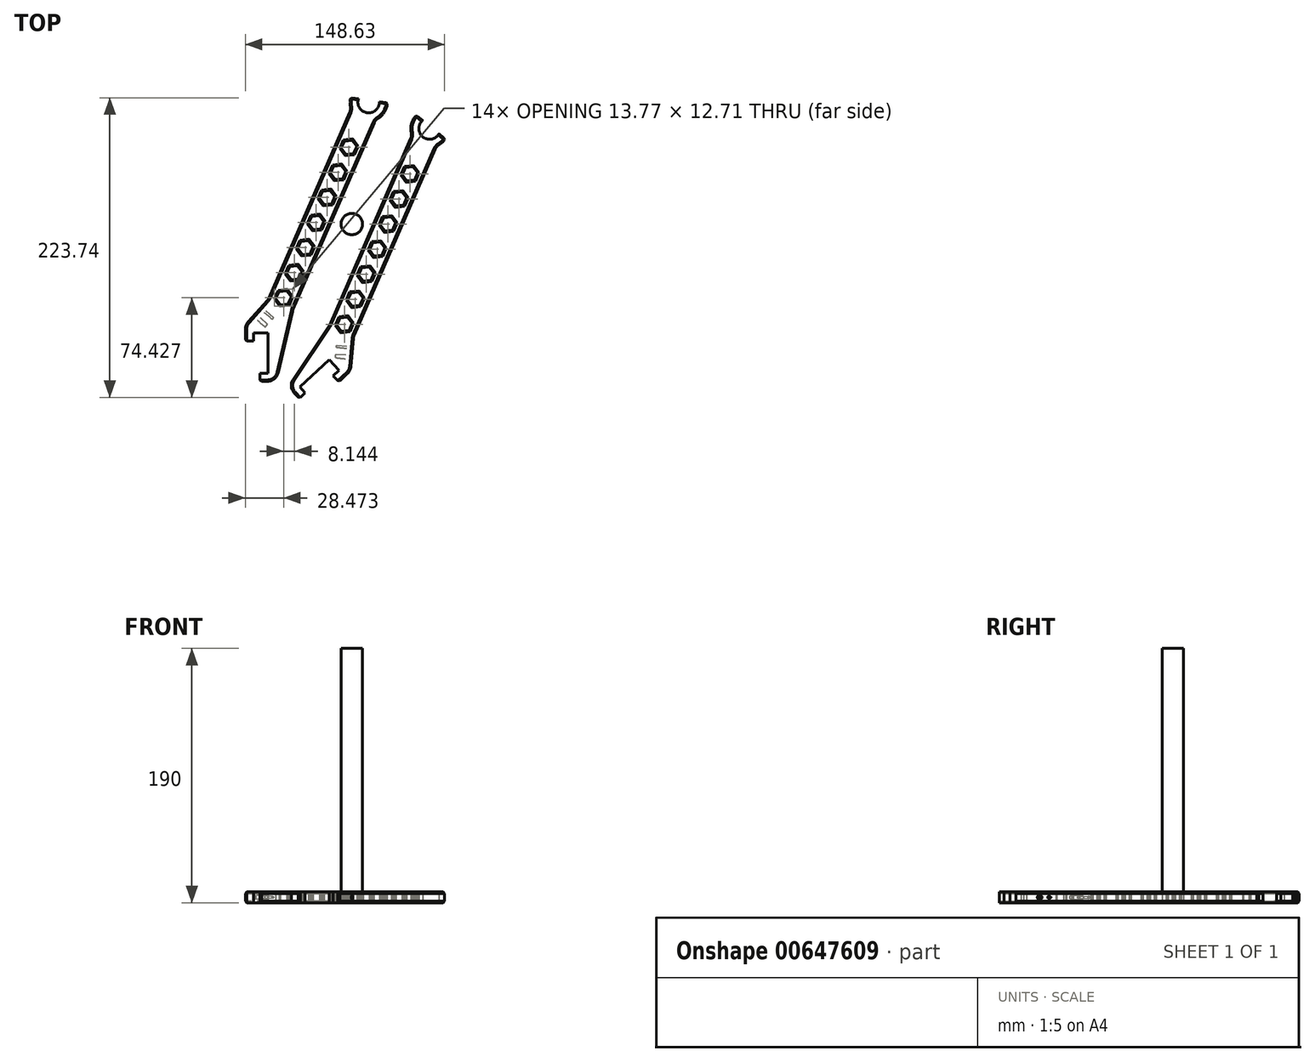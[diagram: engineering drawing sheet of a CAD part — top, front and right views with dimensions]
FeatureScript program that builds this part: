
annotation { "Feature Type Name" : "Feature", "Feature Type Description" : "" }
export const myFeature = defineFeature(function(context is Context, id is Id, definition is map)
    precondition{}
    {
        {
            var Q0;
            Q0=qCreatedBy(makeId("Top.planeOp"),FACE);
            var sketch = newSketch(context, id + "F0", { "sketchPlane" : qUnion([Q0])});
            skLineSegment(sketch, "E0.bottom", {"start": v(6, 6) * mm, "end": v(-17, 6) * mm, "construction": true});
            skLineSegment(sketch, "E0.top", {"start": v(6, -36) * mm, "end": v(-6, -36) * mm});
            skLineSegment(sketch, "E0.left", {"start": v(6, 6) * mm, "end": v(6, -36) * mm, "construction": true});
            skLineSegment(sketch, "E0.right", {"start": v(-17, 6) * mm, "end": v(-17, -6) * mm});
            skLineSegment(sketch, "E1", {"start": v(-17, -6) * mm, "end": v(-11, -6) * mm});
            skLineSegment(sketch, "E2", {"start": v(-11, -6) * mm, "end": v(-11, 0) * mm});
            skLineSegment(sketch, "E3", {"start": v(-11, 0) * mm, "end": v(0, 0) * mm});
            skLineSegment(sketch, "E4", {"start": v(0, 0) * mm, "end": v(0, -30) * mm});
            skLineSegment(sketch, "E5", {"start": v(0, -30) * mm, "end": v(-6, -30) * mm});
            skLineSegment(sketch, "E6", {"start": v(-6, -30) * mm, "end": v(-6, -36) * mm});
            skCircle(sketch, "E7", {"center": v(75, 172.5) * mm, "radius": 8 * mm});
            skCircle(sketch, "E8", {"center": v(75, 172.5) * mm, "radius": 14 * mm});
            skLineSegment(sketch, "E9", {"start": v(61.4, 175.82) * mm, "end": v(89, 172.07) * mm});
            skLineSegment(sketch, "E10", {"start": v(-17, 6) * mm, "end": v(0, 25.08) * mm});
            skLineSegment(sketch, "E11", {"start": v(0, 25.08) * mm, "end": v(61.92, 167.5) * mm});
            skLineSegment(sketch, "E12", {"start": v(18.34, 17.1) * mm, "end": v(6, -36) * mm});
            skLineSegment(sketch, "E13", {"start": v(18.34, 17.1) * mm, "end": v(80.26, 159.53) * mm});
            skLineSegment(sketch, "E14.0", {"start": v(0, 0) * mm, "end": v(75, 172.5) * mm, "construction": true});
            skLineSegment(sketch, "E15", {"start": v(0, 25.08) * mm, "end": v(18.34, 17.1) * mm, "construction": true});
            skCircle(sketch, "E16.cCircle", {"center": v(60.34, 138.78) * mm, "radius": 5.77 * mm, "construction": true});
            skLineSegment(sketch, "E16.0", {"start": v(58.04, 133.48) * mm, "end": v(54.6, 138.12) * mm});
            skLineSegment(sketch, "E16.1", {"start": v(54.6, 138.12) * mm, "end": v(56.9, 143.42) * mm});
            skLineSegment(sketch, "E16.2", {"start": v(56.9, 143.42) * mm, "end": v(62.64, 144.07) * mm});
            skLineSegment(sketch, "E16.3", {"start": v(62.64, 144.07) * mm, "end": v(66.07, 139.43) * mm});
            skLineSegment(sketch, "E16.4", {"start": v(66.07, 139.43) * mm, "end": v(63.77, 134.14) * mm});
            skLineSegment(sketch, "E16.5", {"start": v(63.77, 134.14) * mm, "end": v(58.04, 133.48) * mm});
            skCircle(sketch, "E17.cCircle", {"center": v(44.05, 101.31) * mm, "radius": 5.77 * mm, "construction": true});
            skLineSegment(sketch, "E17.0", {"start": v(41.75, 96.02) * mm, "end": v(38.31, 100.66) * mm});
            skLineSegment(sketch, "E17.1", {"start": v(38.31, 100.66) * mm, "end": v(40.61, 105.95) * mm});
            skLineSegment(sketch, "E17.2", {"start": v(40.61, 105.95) * mm, "end": v(46.35, 106.6) * mm});
            skLineSegment(sketch, "E17.3", {"start": v(46.35, 106.6) * mm, "end": v(49.79, 101.97) * mm});
            skLineSegment(sketch, "E17.4", {"start": v(49.79, 101.97) * mm, "end": v(47.48, 96.67) * mm});
            skLineSegment(sketch, "E17.5", {"start": v(47.48, 96.67) * mm, "end": v(41.75, 96.02) * mm});
            skCircle(sketch, "E18.cCircle", {"center": v(35.9, 82.58) * mm, "radius": 5.77 * mm, "construction": true});
            skLineSegment(sketch, "E18.0", {"start": v(33.6, 77.29) * mm, "end": v(30.17, 81.93) * mm});
            skLineSegment(sketch, "E18.1", {"start": v(30.17, 81.93) * mm, "end": v(32.47, 87.22) * mm});
            skLineSegment(sketch, "E18.2", {"start": v(32.47, 87.22) * mm, "end": v(38.2, 87.88) * mm});
            skLineSegment(sketch, "E18.3", {"start": v(38.2, 87.88) * mm, "end": v(41.64, 83.24) * mm});
            skLineSegment(sketch, "E18.4", {"start": v(41.64, 83.24) * mm, "end": v(39.34, 77.94) * mm});
            skLineSegment(sketch, "E18.5", {"start": v(39.34, 77.94) * mm, "end": v(33.6, 77.29) * mm});
            skCircle(sketch, "E19.cCircle", {"center": v(11.47, 26.39) * mm, "radius": 5.77 * mm, "construction": true});
            skLineSegment(sketch, "E19.0", {"start": v(9.17, 21.1) * mm, "end": v(5.74, 25.73) * mm});
            skLineSegment(sketch, "E19.1", {"start": v(5.74, 25.73) * mm, "end": v(8.04, 31.03) * mm});
            skLineSegment(sketch, "E19.2", {"start": v(8.04, 31.03) * mm, "end": v(13.77, 31.68) * mm});
            skLineSegment(sketch, "E19.3", {"start": v(13.77, 31.68) * mm, "end": v(17.2, 27.04) * mm});
            skLineSegment(sketch, "E19.4", {"start": v(17.2, 27.04) * mm, "end": v(14.9, 21.75) * mm});
            skLineSegment(sketch, "E19.5", {"start": v(14.9, 21.75) * mm, "end": v(9.17, 21.1) * mm});
            skLineSegment(sketch, "E20", {"start": v(62.64, 144.07) * mm, "end": v(71.81, 165.16) * mm, "construction": true});
            skLineSegment(sketch, "E21", {"start": v(9.17, 21.1) * mm, "end": v(0, 0) * mm, "construction": true});
            skCircle(sketch, "E22.cCircle", {"center": v(19.62, 45.12) * mm, "radius": 5.77 * mm, "construction": true});
            skLineSegment(sketch, "E22.0", {"start": v(21.92, 50.41) * mm, "end": v(25.35, 45.77) * mm});
            skLineSegment(sketch, "E22.1", {"start": v(25.35, 45.77) * mm, "end": v(23.05, 40.48) * mm});
            skLineSegment(sketch, "E22.2", {"start": v(23.05, 40.48) * mm, "end": v(17.31, 39.82) * mm});
            skLineSegment(sketch, "E22.3", {"start": v(17.31, 39.82) * mm, "end": v(13.88, 44.47) * mm});
            skLineSegment(sketch, "E22.4", {"start": v(13.88, 44.47) * mm, "end": v(16.18, 49.76) * mm});
            skLineSegment(sketch, "E22.5", {"start": v(16.18, 49.76) * mm, "end": v(21.92, 50.41) * mm});
            skCircle(sketch, "E23.cCircle", {"center": v(27.76, 63.85) * mm, "radius": 5.77 * mm, "construction": true});
            skLineSegment(sketch, "E23.0", {"start": v(30.06, 69.14) * mm, "end": v(33.5, 64.5) * mm});
            skLineSegment(sketch, "E23.1", {"start": v(33.5, 64.5) * mm, "end": v(31.2, 59.2) * mm});
            skLineSegment(sketch, "E23.2", {"start": v(31.2, 59.2) * mm, "end": v(25.46, 58.56) * mm});
            skLineSegment(sketch, "E23.3", {"start": v(25.46, 58.56) * mm, "end": v(22.02, 63.2) * mm});
            skLineSegment(sketch, "E23.4", {"start": v(22.02, 63.2) * mm, "end": v(24.33, 68.5) * mm});
            skLineSegment(sketch, "E23.5", {"start": v(24.33, 68.5) * mm, "end": v(30.06, 69.14) * mm});
            skCircle(sketch, "E24.cCircle", {"center": v(52.2, 120.04) * mm, "radius": 5.77 * mm, "construction": true});
            skLineSegment(sketch, "E24.0", {"start": v(49.9, 114.75) * mm, "end": v(46.46, 119.4) * mm});
            skLineSegment(sketch, "E24.1", {"start": v(46.46, 119.4) * mm, "end": v(48.76, 124.69) * mm});
            skLineSegment(sketch, "E24.2", {"start": v(48.76, 124.69) * mm, "end": v(54.5, 125.34) * mm});
            skLineSegment(sketch, "E24.3", {"start": v(54.5, 125.34) * mm, "end": v(57.93, 120.7) * mm});
            skLineSegment(sketch, "E24.4", {"start": v(57.93, 120.7) * mm, "end": v(55.63, 115.4) * mm});
            skLineSegment(sketch, "E24.5", {"start": v(55.63, 115.4) * mm, "end": v(49.9, 114.75) * mm});
            skLineSegment(sketch, "E25", {"start": v(60.34, 138.78) * mm, "end": v(52.2, 120.04) * mm, "construction": true});
            skLineSegment(sketch, "E26", {"start": v(52.2, 120.04) * mm, "end": v(44.05, 101.31) * mm, "construction": true});
            skLineSegment(sketch, "E27", {"start": v(44.05, 101.31) * mm, "end": v(35.9, 82.58) * mm, "construction": true});
            skLineSegment(sketch, "E28", {"start": v(35.9, 82.58) * mm, "end": v(27.76, 63.85) * mm, "construction": true});
            skLineSegment(sketch, "E29", {"start": v(27.76, 63.85) * mm, "end": v(19.62, 45.12) * mm, "construction": true});
            skLineSegment(sketch, "E30", {"start": v(19.62, 45.12) * mm, "end": v(11.47, 26.39) * mm, "construction": true});
            skSolve(sketch);
        }
        {
            var Q0;
            Q0=makeQuery(id+"F0.imprint","IMPRINT",FACE,{"disambiguationData":[TD([[makeQuery(id+"F0.imprint","IMPRINT",EDGE,{"derivedFrom":sQuery(id+"F0.wireOp",EDGE,"E0.top")}),-1.0]])]});
            var Q1;
            {var subQ0=sQuery(id+"F0.wireOp",EDGE,"E9");var subQ6=sQuery(id+"F0.wireOp",EDGE,"E7");var subQ7=makeQuery(id+"F0.imprint","INTERSECT",VERTEX,{"disambiguationData":[OD(0.0)],"derivedFrom":[subQ6,subQ0]});Q1=makeQuery(id+"F0.imprint","IMPRINT",FACE,{"disambiguationData":[TD([[makeQuery(id+"F0.imprint","IMPRINT",EDGE,{"disambiguationData":[TD([[subQ7,-1.0]])],"derivedFrom":subQ6}),-1.0]])]});}
            extrude(context, id + "F1", {"entities" : qUnion([Q0, Q1]), "depth" : 8 * mm, "offsetDistance" : 25 * mm});
        }
        {
            var Q0;
            Q0=makeQuery(id+"F1.opExtrude","SWEPT_EDGE",EDGE,{"disambiguationData":[OSD([sQuery(id+"F0.wireOp",EDGE,"E0.right"),sQuery(id+"F0.wireOp",EDGE,"E10")])]});
            var Q1;
            Q1=makeQuery(id+"F1.opExtrude","SWEPT_EDGE",EDGE,{"disambiguationData":[OSD([sQuery(id+"F0.wireOp",EDGE,"E10"),sQuery(id+"F0.wireOp",EDGE,"E11")])]});
            var Q2;
            Q2=makeQuery(id+"F1.opExtrude","SWEPT_EDGE",EDGE,{"disambiguationData":[OSD([sQuery(id+"F0.wireOp",EDGE,"E8"),sQuery(id+"F0.wireOp",EDGE,"E11")])]});
            var Q3;
            Q3=makeQuery(id+"F1.opExtrude","SWEPT_EDGE",EDGE,{"disambiguationData":[OSD([sQuery(id+"F0.wireOp",EDGE,"E8"),sQuery(id+"F0.wireOp",EDGE,"E13")])]});
            var Q4;
            Q4=makeQuery(id+"F1.opExtrude","SWEPT_EDGE",EDGE,{"disambiguationData":[OSD([sQuery(id+"F0.wireOp",EDGE,"E12"),sQuery(id+"F0.wireOp",EDGE,"E13")])]});
            var Q5;
            Q5=makeQuery(id+"F1.opExtrude","SWEPT_EDGE",EDGE,{"disambiguationData":[OSD([sQuery(id+"F0.wireOp",EDGE,"E0.top"),sQuery(id+"F0.wireOp",EDGE,"E12")])]});
            fillet(context, id + "F2", {"entities" : qUnion([Q0, Q1, Q2, Q3, Q4, Q5]), "radius" : 8 * mm, "tangentPropagation" : true, "allowEdgeOverflow" : false});
        }
        {
            var Q0;
            Q0=makeQuery(id+"F1.opExtrude","SWEPT_FACE",FACE,{"disambiguationData":[OSD([sQuery(id+"F0.wireOp",EDGE,"E10")])]});
            var sketch = newSketch(context, id + "F3", { "sketchPlane" : qUnion([Q0])});
            skCircle(sketch, "E31", {"center": v(-10.44, 4) * mm, "radius": 0.97 * mm});
            skCircle(sketch, "E32", {"center": v(-3.22, 4) * mm, "radius": 1.6 * mm});
            skLineSegment(sketch, "E33", {"start": v(3.78, 4) * mm, "end": v(-17.44, 4) * mm, "construction": true});
            skSolve(sketch);
        }
        {
            var Q0;
            Q0=makeQuery(id+"F3.imprint","IMPRINT",FACE,{"disambiguationData":[TD([[makeQuery(id+"F3.imprint","IMPRINT",EDGE,{"derivedFrom":sQuery(id+"F3.wireOp",EDGE,"E32")}),1.0]])]});
            var Q1;
            Q1=makeQuery(id+"F3.imprint","IMPRINT",FACE,{"disambiguationData":[TD([[makeQuery(id+"F3.imprint","IMPRINT",EDGE,{"derivedFrom":sQuery(id+"F3.wireOp",EDGE,"E31")}),1.0]])]});
            extrude(context, id + "F4", {"entities" : qUnion([Q0, Q1]), "operationType" : NewBodyOperationType.REMOVE, "oppositeDirection" : true, "depth" : 12 * mm, "offsetDistance" : 25 * mm, "hasDraft" : true, "draftAngle" : 1 * degree, "draftPullDirection" : true});
        }
        {
            var Q0;
            {var subQ0=sQuery(id+"F0.wireOp",EDGE,"E9");Q0=makeQuery(id+"F1.opExtrude","CAP_EDGE",EDGE,{"disambiguationData":[OSD([subQ0]),TDD([makeQuery(id+"F0.imprint","IMPRINT",EDGE,{"disambiguationData":[TD([[makeQuery(id+"F0.imprint","INTERSECT",VERTEX,{"disambiguationData":[OD(0.0)],"derivedFrom":[sQuery(id+"F0.wireOp",EDGE,"E8"),subQ0]}),-1.0]])],"derivedFrom":subQ0})])],"isStart":false});}
            var Q1;
            {var subQ0=sQuery(id+"F0.wireOp",EDGE,"E9");Q1=makeQuery(id+"F1.opExtrude","CAP_EDGE",EDGE,{"disambiguationData":[OSD([subQ0]),TDD([makeQuery(id+"F0.imprint","IMPRINT",EDGE,{"disambiguationData":[TD([[makeQuery(id+"F0.imprint","INTERSECT",VERTEX,{"disambiguationData":[OD(1.0)],"derivedFrom":[sQuery(id+"F0.wireOp",EDGE,"E8"),subQ0]}),1.0]])],"derivedFrom":subQ0})])],"isStart":false});}
            var Q2;
            {var subQ0=sQuery(id+"F0.wireOp",EDGE,"E8");Q2=makeQuery(id+"F1.opExtrude","CAP_EDGE",EDGE,{"disambiguationData":[OSD([subQ0]),TDD([makeQuery(id+"F0.imprint","IMPRINT",EDGE,{"disambiguationData":[TD([[makeQuery(id+"F0.imprint","INTERSECT",VERTEX,{"disambiguationData":[OD(1.0)],"derivedFrom":[subQ0,sQuery(id+"F0.wireOp",EDGE,"E9")]}),1.0]])],"derivedFrom":subQ0})])],"isStart":false});}
            var Q3;
            {var subQ0=sQuery(id+"F0.wireOp",EDGE,"E8");Q3=makeQuery(id+"F1.opExtrude","CAP_EDGE",EDGE,{"disambiguationData":[OSD([subQ0]),TDD([makeQuery(id+"F0.imprint","IMPRINT",EDGE,{"disambiguationData":[TD([[makeQuery(id+"F0.imprint","INTERSECT",VERTEX,{"disambiguationData":[OD(0.0)],"derivedFrom":[subQ0,sQuery(id+"F0.wireOp",EDGE,"E9")]}),-1.0]])],"derivedFrom":subQ0})])],"isStart":false});}
            var Q4;
            Q4=makeQuery(id+"F1.opExtrude","CAP_EDGE",EDGE,{"disambiguationData":[OSD([sQuery(id+"F0.wireOp",EDGE,"E16.2")])],"isStart":false});
            var Q5;
            Q5=makeQuery(id+"F1.opExtrude","CAP_EDGE",EDGE,{"disambiguationData":[OSD([sQuery(id+"F0.wireOp",EDGE,"E16.3")])],"isStart":false});
            var Q6;
            Q6=makeQuery(id+"F1.opExtrude","CAP_EDGE",EDGE,{"disambiguationData":[OSD([sQuery(id+"F0.wireOp",EDGE,"E16.4")])],"isStart":false});
            var Q7;
            Q7=makeQuery(id+"F1.opExtrude","CAP_EDGE",EDGE,{"disambiguationData":[OSD([sQuery(id+"F0.wireOp",EDGE,"E16.5")])],"isStart":false});
            var Q8;
            Q8=makeQuery(id+"F1.opExtrude","CAP_EDGE",EDGE,{"disambiguationData":[OSD([sQuery(id+"F0.wireOp",EDGE,"E16.0")])],"isStart":false});
            var Q9;
            Q9=makeQuery(id+"F1.opExtrude","CAP_EDGE",EDGE,{"disambiguationData":[OSD([sQuery(id+"F0.wireOp",EDGE,"E16.1")])],"isStart":false});
            var Q10;
            Q10=makeQuery(id+"F1.opExtrude","CAP_EDGE",EDGE,{"disambiguationData":[OSD([sQuery(id+"F0.wireOp",EDGE,"E17.2")])],"isStart":false});
            var Q11;
            Q11=makeQuery(id+"F1.opExtrude","CAP_EDGE",EDGE,{"disambiguationData":[OSD([sQuery(id+"F0.wireOp",EDGE,"E17.3")])],"isStart":false});
            var Q12;
            Q12=makeQuery(id+"F1.opExtrude","CAP_EDGE",EDGE,{"disambiguationData":[OSD([sQuery(id+"F0.wireOp",EDGE,"E17.4")])],"isStart":false});
            var Q13;
            Q13=makeQuery(id+"F1.opExtrude","CAP_EDGE",EDGE,{"disambiguationData":[OSD([sQuery(id+"F0.wireOp",EDGE,"E17.5")])],"isStart":false});
            var Q14;
            Q14=makeQuery(id+"F1.opExtrude","CAP_EDGE",EDGE,{"disambiguationData":[OSD([sQuery(id+"F0.wireOp",EDGE,"E17.0")])],"isStart":false});
            var Q15;
            Q15=makeQuery(id+"F1.opExtrude","CAP_EDGE",EDGE,{"disambiguationData":[OSD([sQuery(id+"F0.wireOp",EDGE,"E17.1")])],"isStart":false});
            var Q16;
            Q16=makeQuery(id+"F1.opExtrude","CAP_EDGE",EDGE,{"disambiguationData":[OSD([sQuery(id+"F0.wireOp",EDGE,"E18.3")])],"isStart":false});
            var Q17;
            Q17=makeQuery(id+"F1.opExtrude","CAP_EDGE",EDGE,{"disambiguationData":[OSD([sQuery(id+"F0.wireOp",EDGE,"E18.4")])],"isStart":false});
            var Q18;
            Q18=makeQuery(id+"F1.opExtrude","CAP_EDGE",EDGE,{"disambiguationData":[OSD([sQuery(id+"F0.wireOp",EDGE,"E18.5")])],"isStart":false});
            var Q19;
            Q19=makeQuery(id+"F1.opExtrude","CAP_EDGE",EDGE,{"disambiguationData":[OSD([sQuery(id+"F0.wireOp",EDGE,"E18.0")])],"isStart":false});
            var Q20;
            Q20=makeQuery(id+"F1.opExtrude","CAP_EDGE",EDGE,{"disambiguationData":[OSD([sQuery(id+"F0.wireOp",EDGE,"E18.1")])],"isStart":false});
            var Q21;
            Q21=makeQuery(id+"F1.opExtrude","CAP_EDGE",EDGE,{"disambiguationData":[OSD([sQuery(id+"F0.wireOp",EDGE,"E18.2")])],"isStart":false});
            var Q22;
            Q22=makeQuery(id+"F1.opExtrude","CAP_EDGE",EDGE,{"disambiguationData":[OSD([sQuery(id+"F0.wireOp",EDGE,"E19.2")])],"isStart":false});
            var Q23;
            Q23=makeQuery(id+"F1.opExtrude","CAP_EDGE",EDGE,{"disambiguationData":[OSD([sQuery(id+"F0.wireOp",EDGE,"E19.3")])],"isStart":false});
            var Q24;
            Q24=makeQuery(id+"F1.opExtrude","CAP_EDGE",EDGE,{"disambiguationData":[OSD([sQuery(id+"F0.wireOp",EDGE,"E19.4")])],"isStart":false});
            var Q25;
            Q25=makeQuery(id+"F1.opExtrude","CAP_EDGE",EDGE,{"disambiguationData":[OSD([sQuery(id+"F0.wireOp",EDGE,"E19.5")])],"isStart":false});
            var Q26;
            Q26=makeQuery(id+"F1.opExtrude","CAP_EDGE",EDGE,{"disambiguationData":[OSD([sQuery(id+"F0.wireOp",EDGE,"E19.0")])],"isStart":false});
            var Q27;
            Q27=makeQuery(id+"F1.opExtrude","CAP_EDGE",EDGE,{"disambiguationData":[OSD([sQuery(id+"F0.wireOp",EDGE,"E19.1")])],"isStart":false});
            var Q28;
            {var subQ0=sQuery(id+"F0.wireOp",EDGE,"E9");Q28=makeQuery(id+"F1.opExtrude","CAP_EDGE",EDGE,{"disambiguationData":[OSD([subQ0]),TDD([makeQuery(id+"F0.imprint","IMPRINT",EDGE,{"disambiguationData":[TD([[makeQuery(id+"F0.imprint","INTERSECT",VERTEX,{"disambiguationData":[OD(0.0)],"derivedFrom":[sQuery(id+"F0.wireOp",EDGE,"E8"),subQ0]}),-1.0]])],"derivedFrom":subQ0})])],"isStart":true});}
            var Q29;
            {var subQ0=sQuery(id+"F0.wireOp",EDGE,"E9");Q29=makeQuery(id+"F1.opExtrude","CAP_EDGE",EDGE,{"disambiguationData":[OSD([subQ0]),TDD([makeQuery(id+"F0.imprint","IMPRINT",EDGE,{"disambiguationData":[TD([[makeQuery(id+"F0.imprint","INTERSECT",VERTEX,{"disambiguationData":[OD(1.0)],"derivedFrom":[sQuery(id+"F0.wireOp",EDGE,"E8"),subQ0]}),1.0]])],"derivedFrom":subQ0})])],"isStart":true});}
            var Q30;
            {var subQ0=sQuery(id+"F0.wireOp",EDGE,"E8");Q30=makeQuery(id+"F1.opExtrude","CAP_EDGE",EDGE,{"disambiguationData":[OSD([subQ0]),TDD([makeQuery(id+"F0.imprint","IMPRINT",EDGE,{"disambiguationData":[TD([[makeQuery(id+"F0.imprint","INTERSECT",VERTEX,{"disambiguationData":[OD(1.0)],"derivedFrom":[subQ0,sQuery(id+"F0.wireOp",EDGE,"E9")]}),1.0]])],"derivedFrom":subQ0})])],"isStart":true});}
            var Q31;
            {var subQ0=sQuery(id+"F0.wireOp",EDGE,"E8");Q31=makeQuery(id+"F1.opExtrude","CAP_EDGE",EDGE,{"disambiguationData":[OSD([subQ0]),TDD([makeQuery(id+"F0.imprint","IMPRINT",EDGE,{"disambiguationData":[TD([[makeQuery(id+"F0.imprint","INTERSECT",VERTEX,{"disambiguationData":[OD(0.0)],"derivedFrom":[subQ0,sQuery(id+"F0.wireOp",EDGE,"E9")]}),-1.0]])],"derivedFrom":subQ0})])],"isStart":true});}
            var Q32;
            Q32=makeQuery(id+"F1.opExtrude","CAP_EDGE",EDGE,{"disambiguationData":[OSD([sQuery(id+"F0.wireOp",EDGE,"E16.3")])],"isStart":true});
            var Q33;
            Q33=makeQuery(id+"F1.opExtrude","CAP_EDGE",EDGE,{"disambiguationData":[OSD([sQuery(id+"F0.wireOp",EDGE,"E16.2")])],"isStart":true});
            var Q34;
            Q34=makeQuery(id+"F1.opExtrude","CAP_EDGE",EDGE,{"disambiguationData":[OSD([sQuery(id+"F0.wireOp",EDGE,"E16.1")])],"isStart":true});
            var Q35;
            Q35=makeQuery(id+"F1.opExtrude","CAP_EDGE",EDGE,{"disambiguationData":[OSD([sQuery(id+"F0.wireOp",EDGE,"E16.0")])],"isStart":true});
            var Q36;
            Q36=makeQuery(id+"F1.opExtrude","CAP_EDGE",EDGE,{"disambiguationData":[OSD([sQuery(id+"F0.wireOp",EDGE,"E16.5")])],"isStart":true});
            var Q37;
            Q37=makeQuery(id+"F1.opExtrude","CAP_EDGE",EDGE,{"disambiguationData":[OSD([sQuery(id+"F0.wireOp",EDGE,"E16.4")])],"isStart":true});
            var Q38;
            Q38=makeQuery(id+"F1.opExtrude","CAP_EDGE",EDGE,{"disambiguationData":[OSD([sQuery(id+"F0.wireOp",EDGE,"E17.4")])],"isStart":true});
            var Q39;
            Q39=makeQuery(id+"F1.opExtrude","CAP_EDGE",EDGE,{"disambiguationData":[OSD([sQuery(id+"F0.wireOp",EDGE,"E17.3")])],"isStart":true});
            var Q40;
            Q40=makeQuery(id+"F1.opExtrude","CAP_EDGE",EDGE,{"disambiguationData":[OSD([sQuery(id+"F0.wireOp",EDGE,"E17.2")])],"isStart":true});
            var Q41;
            Q41=makeQuery(id+"F1.opExtrude","CAP_EDGE",EDGE,{"disambiguationData":[OSD([sQuery(id+"F0.wireOp",EDGE,"E17.1")])],"isStart":true});
            var Q42;
            Q42=makeQuery(id+"F1.opExtrude","CAP_EDGE",EDGE,{"disambiguationData":[OSD([sQuery(id+"F0.wireOp",EDGE,"E17.0")])],"isStart":true});
            var Q43;
            Q43=makeQuery(id+"F1.opExtrude","CAP_EDGE",EDGE,{"disambiguationData":[OSD([sQuery(id+"F0.wireOp",EDGE,"E17.5")])],"isStart":true});
            var Q44;
            Q44=makeQuery(id+"F1.opExtrude","CAP_EDGE",EDGE,{"disambiguationData":[OSD([sQuery(id+"F0.wireOp",EDGE,"E18.4")])],"isStart":true});
            var Q45;
            Q45=makeQuery(id+"F1.opExtrude","CAP_EDGE",EDGE,{"disambiguationData":[OSD([sQuery(id+"F0.wireOp",EDGE,"E18.3")])],"isStart":true});
            var Q46;
            Q46=makeQuery(id+"F1.opExtrude","CAP_EDGE",EDGE,{"disambiguationData":[OSD([sQuery(id+"F0.wireOp",EDGE,"E18.2")])],"isStart":true});
            var Q47;
            Q47=makeQuery(id+"F1.opExtrude","CAP_EDGE",EDGE,{"disambiguationData":[OSD([sQuery(id+"F0.wireOp",EDGE,"E18.1")])],"isStart":true});
            var Q48;
            Q48=makeQuery(id+"F1.opExtrude","CAP_EDGE",EDGE,{"disambiguationData":[OSD([sQuery(id+"F0.wireOp",EDGE,"E18.0")])],"isStart":true});
            var Q49;
            Q49=makeQuery(id+"F1.opExtrude","CAP_EDGE",EDGE,{"disambiguationData":[OSD([sQuery(id+"F0.wireOp",EDGE,"E18.5")])],"isStart":true});
            var Q50;
            Q50=makeQuery(id+"F1.opExtrude","CAP_EDGE",EDGE,{"disambiguationData":[OSD([sQuery(id+"F0.wireOp",EDGE,"E19.3")])],"isStart":true});
            var Q51;
            Q51=makeQuery(id+"F1.opExtrude","CAP_EDGE",EDGE,{"disambiguationData":[OSD([sQuery(id+"F0.wireOp",EDGE,"E19.4")])],"isStart":true});
            var Q52;
            Q52=makeQuery(id+"F1.opExtrude","CAP_EDGE",EDGE,{"disambiguationData":[OSD([sQuery(id+"F0.wireOp",EDGE,"E19.5")])],"isStart":true});
            var Q53;
            Q53=makeQuery(id+"F1.opExtrude","CAP_EDGE",EDGE,{"disambiguationData":[OSD([sQuery(id+"F0.wireOp",EDGE,"E19.0")])],"isStart":true});
            var Q54;
            Q54=makeQuery(id+"F1.opExtrude","CAP_EDGE",EDGE,{"disambiguationData":[OSD([sQuery(id+"F0.wireOp",EDGE,"E19.1")])],"isStart":true});
            var Q55;
            Q55=makeQuery(id+"F1.opExtrude","CAP_EDGE",EDGE,{"disambiguationData":[OSD([sQuery(id+"F0.wireOp",EDGE,"E19.2")])],"isStart":true});
            var Q56;
            Q56=makeQuery(id+"F4.boolean.opBoolean","COPY",EDGE,{"derivedFrom":makeQuery(id+"F4.opExtrude","CAP_EDGE",EDGE,{"disambiguationData":[OSD([sQuery(id+"F3.wireOp",EDGE,"E32")])],"isStart":true})});
            var Q57;
            Q57=makeQuery(id+"F4.boolean.opBoolean","COPY",EDGE,{"derivedFrom":makeQuery(id+"F4.opExtrude","CAP_EDGE",EDGE,{"disambiguationData":[OSD([sQuery(id+"F3.wireOp",EDGE,"E31")])],"isStart":true})});
            var Q58;
            Q58=makeQuery(id+"F1.opExtrude","SWEPT_EDGE",EDGE,{"disambiguationData":[OSD([sQuery(id+"F0.wireOp",EDGE,"E0.right"),sQuery(id+"F0.wireOp",EDGE,"E1")])]});
            var Q59;
            Q59=makeQuery(id+"F1.opExtrude","SWEPT_EDGE",EDGE,{"disambiguationData":[OSD([sQuery(id+"F0.wireOp",EDGE,"E0.top"),sQuery(id+"F0.wireOp",EDGE,"E6")])]});
            var Q60;
            {var subQ0=sQuery(id+"F0.wireOp",EDGE,"E9");var subQ1=sQuery(id+"F0.wireOp",EDGE,"E8");Q60=makeQuery(id+"F1.opExtrude","SWEPT_EDGE",EDGE,{"disambiguationData":[OSD([subQ1,subQ0]),TDD([makeQuery(id+"F0.imprint","INTERSECT",VERTEX,{"disambiguationData":[OD(1.0)],"derivedFrom":[subQ1,subQ0]})])]});}
            var Q61;
            {var subQ0=sQuery(id+"F0.wireOp",EDGE,"E9");var subQ1=sQuery(id+"F0.wireOp",EDGE,"E8");Q61=makeQuery(id+"F1.opExtrude","SWEPT_EDGE",EDGE,{"disambiguationData":[OSD([subQ1,subQ0]),TDD([makeQuery(id+"F0.imprint","INTERSECT",VERTEX,{"disambiguationData":[OD(0.0)],"derivedFrom":[subQ1,subQ0]})])]});}
            var Q62;
            Q62=makeQuery(id+"F1.opExtrude","CAP_EDGE",EDGE,{"disambiguationData":[OSD([sQuery(id+"F0.wireOp",EDGE,"E24.2")])],"isStart":false});
            var Q63;
            Q63=makeQuery(id+"F1.opExtrude","CAP_EDGE",EDGE,{"disambiguationData":[OSD([sQuery(id+"F0.wireOp",EDGE,"E24.3")])],"isStart":false});
            var Q64;
            Q64=makeQuery(id+"F1.opExtrude","CAP_EDGE",EDGE,{"disambiguationData":[OSD([sQuery(id+"F0.wireOp",EDGE,"E24.4")])],"isStart":false});
            var Q65;
            Q65=makeQuery(id+"F1.opExtrude","CAP_EDGE",EDGE,{"disambiguationData":[OSD([sQuery(id+"F0.wireOp",EDGE,"E24.5")])],"isStart":false});
            var Q66;
            Q66=makeQuery(id+"F1.opExtrude","CAP_EDGE",EDGE,{"disambiguationData":[OSD([sQuery(id+"F0.wireOp",EDGE,"E24.0")])],"isStart":false});
            var Q67;
            Q67=makeQuery(id+"F1.opExtrude","CAP_EDGE",EDGE,{"disambiguationData":[OSD([sQuery(id+"F0.wireOp",EDGE,"E24.1")])],"isStart":false});
            var Q68;
            Q68=makeQuery(id+"F1.opExtrude","CAP_EDGE",EDGE,{"disambiguationData":[OSD([sQuery(id+"F0.wireOp",EDGE,"E23.0")])],"isStart":false});
            var Q69;
            Q69=makeQuery(id+"F1.opExtrude","CAP_EDGE",EDGE,{"disambiguationData":[OSD([sQuery(id+"F0.wireOp",EDGE,"E23.5")])],"isStart":false});
            var Q70;
            Q70=makeQuery(id+"F1.opExtrude","CAP_EDGE",EDGE,{"disambiguationData":[OSD([sQuery(id+"F0.wireOp",EDGE,"E23.4")])],"isStart":false});
            var Q71;
            Q71=makeQuery(id+"F1.opExtrude","CAP_EDGE",EDGE,{"disambiguationData":[OSD([sQuery(id+"F0.wireOp",EDGE,"E23.3")])],"isStart":false});
            var Q72;
            Q72=makeQuery(id+"F1.opExtrude","CAP_EDGE",EDGE,{"disambiguationData":[OSD([sQuery(id+"F0.wireOp",EDGE,"E23.2")])],"isStart":false});
            var Q73;
            Q73=makeQuery(id+"F1.opExtrude","CAP_EDGE",EDGE,{"disambiguationData":[OSD([sQuery(id+"F0.wireOp",EDGE,"E23.1")])],"isStart":false});
            var Q74;
            Q74=makeQuery(id+"F1.opExtrude","CAP_EDGE",EDGE,{"disambiguationData":[OSD([sQuery(id+"F0.wireOp",EDGE,"E22.0")])],"isStart":false});
            var Q75;
            Q75=makeQuery(id+"F1.opExtrude","CAP_EDGE",EDGE,{"disambiguationData":[OSD([sQuery(id+"F0.wireOp",EDGE,"E22.5")])],"isStart":false});
            var Q76;
            Q76=makeQuery(id+"F1.opExtrude","CAP_EDGE",EDGE,{"disambiguationData":[OSD([sQuery(id+"F0.wireOp",EDGE,"E22.4")])],"isStart":false});
            var Q77;
            Q77=makeQuery(id+"F1.opExtrude","CAP_EDGE",EDGE,{"disambiguationData":[OSD([sQuery(id+"F0.wireOp",EDGE,"E22.3")])],"isStart":false});
            var Q78;
            Q78=makeQuery(id+"F1.opExtrude","CAP_EDGE",EDGE,{"disambiguationData":[OSD([sQuery(id+"F0.wireOp",EDGE,"E22.2")])],"isStart":false});
            var Q79;
            Q79=makeQuery(id+"F1.opExtrude","CAP_EDGE",EDGE,{"disambiguationData":[OSD([sQuery(id+"F0.wireOp",EDGE,"E22.1")])],"isStart":false});
            var Q80;
            Q80=makeQuery(id+"F1.opExtrude","CAP_EDGE",EDGE,{"disambiguationData":[OSD([sQuery(id+"F0.wireOp",EDGE,"E22.4")])],"isStart":true});
            var Q81;
            Q81=makeQuery(id+"F1.opExtrude","CAP_EDGE",EDGE,{"disambiguationData":[OSD([sQuery(id+"F0.wireOp",EDGE,"E22.3")])],"isStart":true});
            var Q82;
            Q82=makeQuery(id+"F1.opExtrude","CAP_EDGE",EDGE,{"disambiguationData":[OSD([sQuery(id+"F0.wireOp",EDGE,"E22.2")])],"isStart":true});
            var Q83;
            Q83=makeQuery(id+"F1.opExtrude","CAP_EDGE",EDGE,{"disambiguationData":[OSD([sQuery(id+"F0.wireOp",EDGE,"E22.1")])],"isStart":true});
            var Q84;
            Q84=makeQuery(id+"F1.opExtrude","CAP_EDGE",EDGE,{"disambiguationData":[OSD([sQuery(id+"F0.wireOp",EDGE,"E22.0")])],"isStart":true});
            var Q85;
            Q85=makeQuery(id+"F1.opExtrude","CAP_EDGE",EDGE,{"disambiguationData":[OSD([sQuery(id+"F0.wireOp",EDGE,"E22.5")])],"isStart":true});
            var Q86;
            Q86=makeQuery(id+"F1.opExtrude","CAP_EDGE",EDGE,{"disambiguationData":[OSD([sQuery(id+"F0.wireOp",EDGE,"E23.3")])],"isStart":true});
            var Q87;
            Q87=makeQuery(id+"F1.opExtrude","CAP_EDGE",EDGE,{"disambiguationData":[OSD([sQuery(id+"F0.wireOp",EDGE,"E23.2")])],"isStart":true});
            var Q88;
            Q88=makeQuery(id+"F1.opExtrude","CAP_EDGE",EDGE,{"disambiguationData":[OSD([sQuery(id+"F0.wireOp",EDGE,"E23.1")])],"isStart":true});
            var Q89;
            Q89=makeQuery(id+"F1.opExtrude","CAP_EDGE",EDGE,{"disambiguationData":[OSD([sQuery(id+"F0.wireOp",EDGE,"E23.0")])],"isStart":true});
            var Q90;
            Q90=makeQuery(id+"F1.opExtrude","CAP_EDGE",EDGE,{"disambiguationData":[OSD([sQuery(id+"F0.wireOp",EDGE,"E23.5")])],"isStart":true});
            var Q91;
            Q91=makeQuery(id+"F1.opExtrude","CAP_EDGE",EDGE,{"disambiguationData":[OSD([sQuery(id+"F0.wireOp",EDGE,"E23.4")])],"isStart":true});
            var Q92;
            Q92=makeQuery(id+"F1.opExtrude","CAP_EDGE",EDGE,{"disambiguationData":[OSD([sQuery(id+"F0.wireOp",EDGE,"E24.5")])],"isStart":true});
            var Q93;
            Q93=makeQuery(id+"F1.opExtrude","CAP_EDGE",EDGE,{"disambiguationData":[OSD([sQuery(id+"F0.wireOp",EDGE,"E24.4")])],"isStart":true});
            var Q94;
            Q94=makeQuery(id+"F1.opExtrude","CAP_EDGE",EDGE,{"disambiguationData":[OSD([sQuery(id+"F0.wireOp",EDGE,"E24.3")])],"isStart":true});
            var Q95;
            Q95=makeQuery(id+"F1.opExtrude","CAP_EDGE",EDGE,{"disambiguationData":[OSD([sQuery(id+"F0.wireOp",EDGE,"E24.2")])],"isStart":true});
            var Q96;
            Q96=makeQuery(id+"F1.opExtrude","CAP_EDGE",EDGE,{"disambiguationData":[OSD([sQuery(id+"F0.wireOp",EDGE,"E24.1")])],"isStart":true});
            var Q97;
            Q97=makeQuery(id+"F1.opExtrude","CAP_EDGE",EDGE,{"disambiguationData":[OSD([sQuery(id+"F0.wireOp",EDGE,"E24.0")])],"isStart":true});
            chamfer(context, id + "F5", {"entities" : qUnion([Q0, Q1, Q2, Q3, Q4, Q5, Q6, Q7, Q8, Q9, Q10, Q11, Q12, Q13, Q14, Q15, Q16, Q17, Q18, Q19, Q20, Q21, Q22, Q23, Q24, Q25, Q26, Q27, Q28, Q29, Q30, Q31, Q32, Q33, Q34, Q35, Q36, Q37, Q38, Q39, Q40, Q41, Q42, Q43, Q44, Q45, Q46, Q47, Q48, Q49, Q50, Q51, Q52, Q53, Q54, Q55, Q56, Q57, Q58, Q59, Q60, Q61, Q62, Q63, Q64, Q65, Q66, Q67, Q68, Q69, Q70, Q71, Q72, Q73, Q74, Q75, Q76, Q77, Q78, Q79, Q80, Q81, Q82, Q83, Q84, Q85, Q86, Q87, Q88, Q89, Q90, Q91, Q92, Q93, Q94, Q95, Q96, Q97]), "width" : 1 * mm, "tangentPropagation" : true});
        }
        {
            var Q0;
            Q0=makeQuery(id+"F1.opExtrude","SWEPT_FACE",FACE,{"disambiguationData":[OSD([sQuery(id+"F0.wireOp",EDGE,"E13")])]});
            cPlane(context, id + "F6", {"entities" : qUnion([Q0]), "cplaneType" : CPlaneType.OFFSET, "offset" : 14.8 * mm, "width" : 150 * mm, "height" : 150 * mm});
        }
        {
            var Q0;
            Q0=makeQuery(id+"F1.opExtrude","SWEPT_BODY",BODY,{"disambiguationData":[OSD([sQuery(id+"F0.wireOp",EDGE,"E0.top"),sQuery(id+"F0.wireOp",EDGE,"E0.right"),sQuery(id+"F0.wireOp",EDGE,"E1"),sQuery(id+"F0.wireOp",EDGE,"E2"),sQuery(id+"F0.wireOp",EDGE,"E3"),sQuery(id+"F0.wireOp",EDGE,"E4"),sQuery(id+"F0.wireOp",EDGE,"E5"),sQuery(id+"F0.wireOp",EDGE,"E6"),sQuery(id+"F0.wireOp",EDGE,"E7"),sQuery(id+"F0.wireOp",EDGE,"E8"),sQuery(id+"F0.wireOp",EDGE,"E9"),sQuery(id+"F0.wireOp",EDGE,"E10"),sQuery(id+"F0.wireOp",EDGE,"E11"),sQuery(id+"F0.wireOp",EDGE,"E12"),sQuery(id+"F0.wireOp",EDGE,"E13"),sQuery(id+"F0.wireOp",EDGE,"E16.0"),sQuery(id+"F0.wireOp",EDGE,"E16.1"),sQuery(id+"F0.wireOp",EDGE,"E16.2"),sQuery(id+"F0.wireOp",EDGE,"E16.3"),sQuery(id+"F0.wireOp",EDGE,"E16.4"),sQuery(id+"F0.wireOp",EDGE,"E16.5"),sQuery(id+"F0.wireOp",EDGE,"E17.0"),sQuery(id+"F0.wireOp",EDGE,"E17.1"),sQuery(id+"F0.wireOp",EDGE,"E17.2"),sQuery(id+"F0.wireOp",EDGE,"E17.3"),sQuery(id+"F0.wireOp",EDGE,"E17.4"),sQuery(id+"F0.wireOp",EDGE,"E17.5"),sQuery(id+"F0.wireOp",EDGE,"E18.0"),sQuery(id+"F0.wireOp",EDGE,"E18.1"),sQuery(id+"F0.wireOp",EDGE,"E18.2"),sQuery(id+"F0.wireOp",EDGE,"E18.3"),sQuery(id+"F0.wireOp",EDGE,"E18.4"),sQuery(id+"F0.wireOp",EDGE,"E18.5"),sQuery(id+"F0.wireOp",EDGE,"E19.0"),sQuery(id+"F0.wireOp",EDGE,"E19.1"),sQuery(id+"F0.wireOp",EDGE,"E19.2"),sQuery(id+"F0.wireOp",EDGE,"E19.3"),sQuery(id+"F0.wireOp",EDGE,"E19.4"),sQuery(id+"F0.wireOp",EDGE,"E19.5")])]});
            var Q1;
            Q1=qCreatedBy(id+"F6.planeOp",FACE);
            mirror(context, id + "F7", {"entities" : qUnion([Q0]), "mirrorPlane" : qUnion([Q1])});
        }
        {
            var Q0;
            Q0=qCreatedBy(makeId("Top.planeOp"),FACE);
            var sketch = newSketch(context, id + "F8", { "sketchPlane" : qUnion([Q0])});
            skCircle(sketch, "E34", {"center": v(62.45, 81.44) * mm, "radius": 8 * mm});
            skLineSegment(sketch, "E35", {"start": v(48.88, 87.34) * mm, "end": v(76.02, 75.54) * mm, "construction": true});
            skSolve(sketch);
        }
        {
            var Q0;
            Q0=makeQuery(id+"F8.imprint","IMPRINT",FACE,{"disambiguationData":[TD([[makeQuery(id+"F8.imprint","IMPRINT",EDGE,{"derivedFrom":sQuery(id+"F8.wireOp",EDGE,"E34")}),1.0]])]});
            extrude(context, id + "F9", {"entities" : qUnion([Q0]), "depth" : 190 * mm, "offsetDistance" : 25 * mm});
        }
    });
